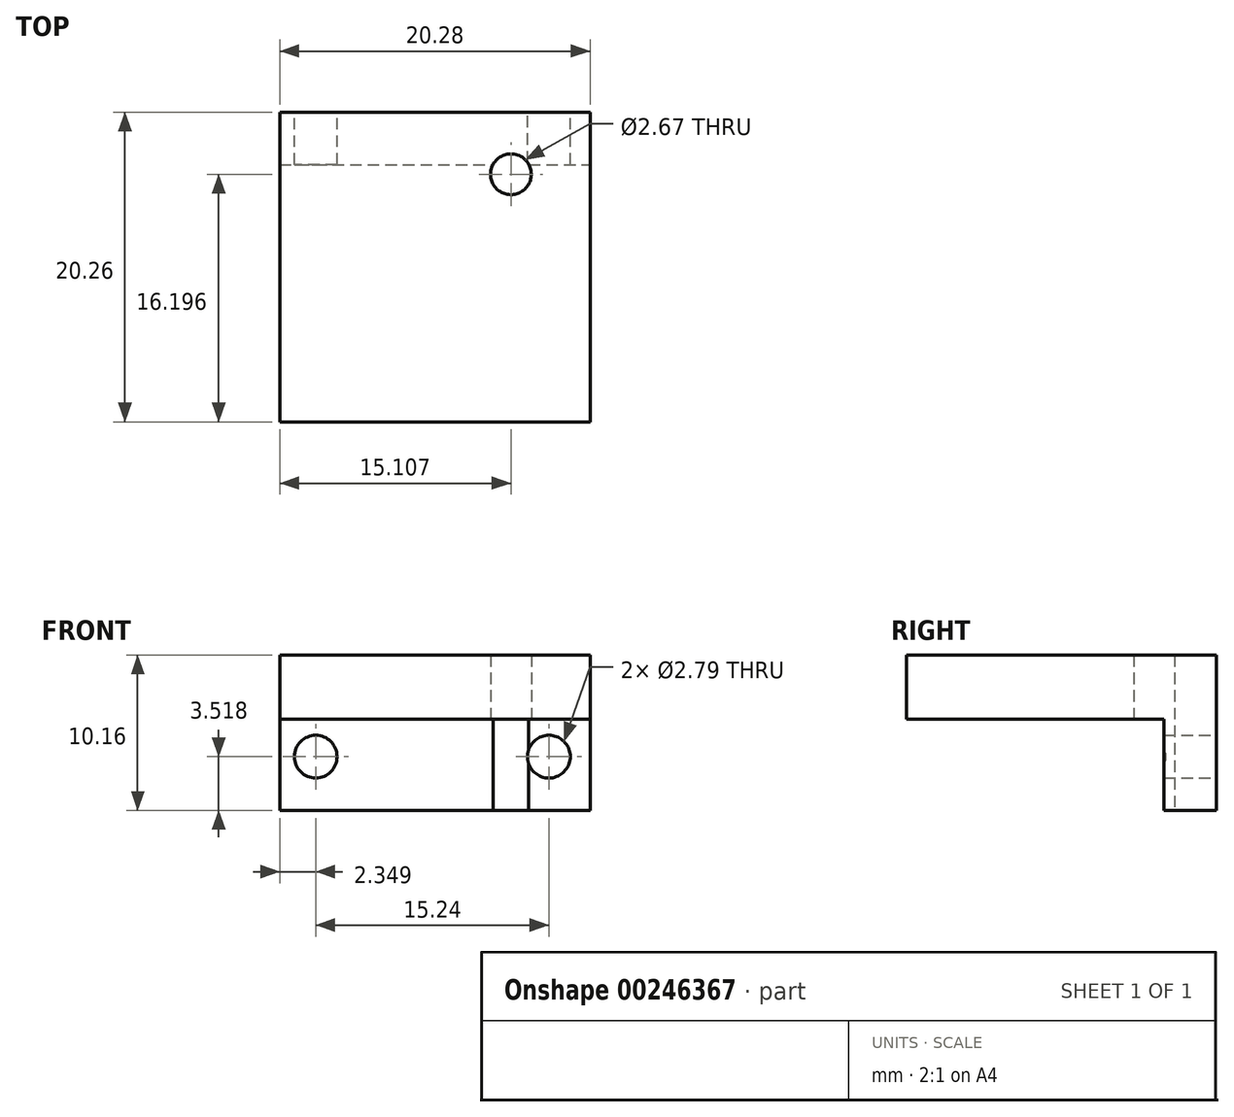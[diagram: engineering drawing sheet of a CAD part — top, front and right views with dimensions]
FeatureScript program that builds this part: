
annotation { "Feature Type Name" : "Feature", "Feature Type Description" : "" }
export const myFeature = defineFeature(function(context is Context, id is Id, definition is map)
    precondition{}
    {
        {
            var Q0;
            Q0=qCreatedBy(makeId("Front.planeOp"),FACE);
            var sketch = newSketch(context, id + "F0", { "sketchPlane" : qUnion([Q0])});
            skLineSegment(sketch, "E0.bottom", {"start": v(0, 0) * mm, "end": v(20.28, 0) * mm});
            skLineSegment(sketch, "E0.top", {"start": v(0, 10.16) * mm, "end": v(20.28, 10.16) * mm});
            skLineSegment(sketch, "E0.left", {"start": v(0, 0) * mm, "end": v(0, 10.16) * mm});
            skLineSegment(sketch, "E0.right", {"start": v(20.28, 0) * mm, "end": v(20.28, 10.16) * mm});
            skPoint(sketch, "E1", {"position": v(2.35, 3.52) * mm});
            skPoint(sketch, "E2", {"position": v(17.59, 3.52) * mm});
            skLineSegment(sketch, "E3", {"start": v(2.35, 3.52) * mm, "end": v(17.59, 3.52) * mm});
            skLineSegment(sketch, "E4", {"start": v(9.97, 3.52) * mm, "end": v(9.97, 2.5) * mm});
            skLineSegment(sketch, "E5", {"start": v(10.14, 10.16) * mm, "end": v(10.14, 7.92) * mm});
            skCircle(sketch, "E6", {"center": v(2.35, 3.52) * mm, "radius": 1.4 * mm});
            skCircle(sketch, "E7", {"center": v(17.59, 3.52) * mm, "radius": 1.4 * mm});
            skSolve(sketch);
        }
        {
            var Q0;
            Q0 = qSketchRegion(id + "F0", true);
            extrude(context, id + "F1", {"entities" : qUnion([Q0]), "depth" : 3.43 * mm});
        }
        {
            var Q0;
            Q0=makeQuery(id+"F1.opExtrude","CAP_FACE",FACE,{"disambiguationData":[OSD([sQuery(id+"F0.wireOp",EDGE,"E0.bottom"),sQuery(id+"F0.wireOp",EDGE,"E0.top"),sQuery(id+"F0.wireOp",EDGE,"E0.left"),sQuery(id+"F0.wireOp",EDGE,"E0.right"),sQuery(id+"F0.wireOp",EDGE,"E6"),sQuery(id+"F0.wireOp",EDGE,"E7")])],"isStart":false});
            var sketch = newSketch(context, id + "F2", { "sketchPlane" : qUnion([Q0])});
            skLineSegment(sketch, "E8.bottom", {"start": v(0, 5.97) * mm, "end": v(20.28, 5.97) * mm});
            skLineSegment(sketch, "E8.top", {"start": v(0, 10.16) * mm, "end": v(20.28, 10.16) * mm});
            skLineSegment(sketch, "E8.left", {"start": v(0, 5.97) * mm, "end": v(0, 10.16) * mm});
            skLineSegment(sketch, "E8.right", {"start": v(20.28, 5.97) * mm, "end": v(20.28, 10.16) * mm});
            skSolve(sketch);
        }
        {
            var Q0;
            Q0=makeQuery(id+"F2.imprint","IMPRINT",FACE,{"disambiguationData":[TD([[makeQuery(id+"F2.imprint","IMPRINT",EDGE,{"derivedFrom":sQuery(id+"F2.wireOp",EDGE,"E8.bottom")}),1.0]])]});
            extrude(context, id + "F3", {"entities" : qUnion([Q0]), "operationType" : NewBodyOperationType.ADD, "depth" : 16.83 * mm});
        }
        {
            var Q0;
            Q0=makeQuery(id+"F3.opExtrude","SWEPT_FACE",FACE,{"disambiguationData":[OSD([sQuery(id+"F2.wireOp",EDGE,"E8.bottom")])]});
            var sketch = newSketch(context, id + "F4", { "sketchPlane" : qUnion([Q0])});
            skLineSegment(sketch, "E9", {"start": v(10.14, 20.26) * mm, "end": v(10.14, 8.94) * mm});
            skCircle(sketch, "E10", {"center": v(15.1, 4.06) * mm, "radius": 1.33 * mm});
            skSolve(sketch);
        }
        {
            var Q0;
            Q0 = qSketchRegion(id + "F4", true);
            extrude(context, id + "F5", {"entities" : qUnion([Q0]), "operationType" : NewBodyOperationType.REMOVE, "endBound" : BoundingType.SYMMETRIC, "oppositeDirection" : true, "depth" : 25.4 * mm});
        }
    });
